# Revit family: Lighting_Linear_LED_Startek_MicroBeam-Direct-Indirect_Ceiling-Mount
name_source: partatom
category: Lighting Fixtures
units: mm (PartAtom-declared; Revit-internal decimal feet)

## family parameters
Cut with Voids When Loaded = Yes
Host = Face
Light Source = Yes
OmniClass Number = 23.80.70.11
OmniClass Title = Luminaries for Internal Lighting
Part Type = Normal
Room Calculation Point = No
Round Connector Dimension = Use Diameter
Shared = No

## types (1)
- Not a Type - Load Type Catalog!
    Apparent Load = 35 VA
    Assembly Code = D5020200
    Color Filter = 16777215
    Default Elevation = 48 "
    Description = Micro Beam Direct-Indirect
    Dimming Lamp Color Temperature Shift = <None>
    Emit Shape Visible in Rendering = No
    Emit from Rectangle Length = 47.88 "
    Emit from Rectangle Width = 1.5 "
    Frequency = 60 Hz
    Height = 1.25 "
    Input Wattage = 33 W
    Keynote = 16500
    Lamp = LED
    Lamp length 4' = Yes
    Lamp length 8' = No
    Length = 48 "
    Manufacturer = StarTek Lighting
    Number of Poles = 1
    Phase = 1
    Photometric Note = Import IES files https://starteklightingamerica.com
    Photometric Web File = Generic Light Source Shown : Please download and link the IES file that best matches your fixture specification
    Power Factor = 0.93
    Product Guid = 1cccbbba-c459-4a37-a225-4308e0dc9aea
    Product data url = https://www.bimobject.com
    Tilt Angle = 90.00°
    Type Comments = Linear Lighting Fixture
    URL = https://starteklightingamerica.com
    Voltage = 120 V
    Voltage Range = 120-277V
    Wattage Comments = Efficacy up to 130 lm/W
    Weight = 0.00 lbf
    Width = 1.25 "
    z_Cord_distance = 23.73 "
    z_Mounting_CPx = Aircraft Cable : Powered Canopy (PCx)
    z_Mounting_RIW = Aircraft Cable : Remote In-Wall with Canopy (RIWx)
    z_Mounting_RSM = Aircraft Cable : Remote Surface Mount with Canopy (RSMx)

## geometry (parser evidence)
native form markers: Sweep x4
no freeform markers — native parametric forms only
